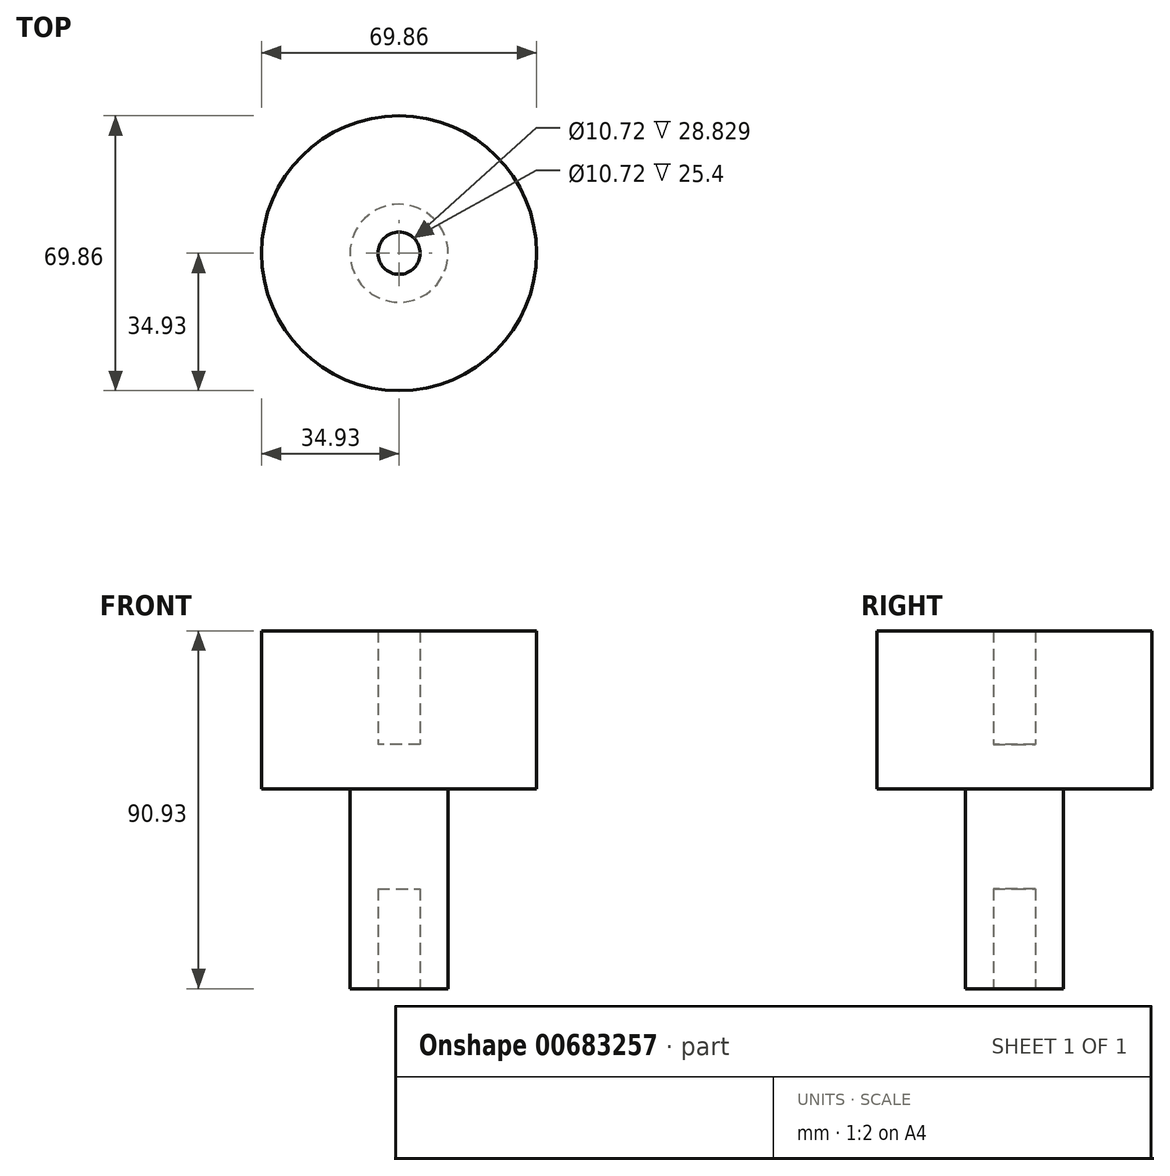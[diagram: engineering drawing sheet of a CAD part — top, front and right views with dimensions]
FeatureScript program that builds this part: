
annotation { "Feature Type Name" : "Feature", "Feature Type Description" : "" }
export const myFeature = defineFeature(function(context is Context, id is Id, definition is map)
    precondition{}
    {
        {
            var Q0;
            Q0=qCreatedBy(makeId("Top.planeOp"),FACE);
            var sketch = newSketch(context, id + "F0", { "sketchPlane" : qUnion([Q0])});
            skCircle(sketch, "E0", {"center": v(0, 0) * mm, "radius": 34.93 * mm});
            skCircle(sketch, "E1", {"center": v(0, 0) * mm, "radius": 5.36 * mm});
            skSolve(sketch);
        }
        {
            var Q0;
            Q0=makeQuery(id+"F0.imprint","IMPRINT",FACE,{"disambiguationData":[TD([[makeQuery(id+"F0.imprint","IMPRINT",EDGE,{"derivedFrom":sQuery(id+"F0.wireOp",EDGE,"E0")}),1.0]])]});
            extrude(context, id + "F1", {"entities" : qUnion([Q0]), "depth" : 40.13 * mm, "offsetDistance" : 25.4 * mm});
        }
        {
            var Q0;
            Q0=makeQuery(id+"F0.imprint","IMPRINT",FACE,{"disambiguationData":[TD([[makeQuery(id+"F0.imprint","IMPRINT",EDGE,{"derivedFrom":sQuery(id+"F0.wireOp",EDGE,"E1")}),1.0]])]});
            extrude(context, id + "F2", {"entities" : qUnion([Q0]), "operationType" : NewBodyOperationType.ADD, "depth" : 9.52 * mm, "offsetDistance" : 25.4 * mm});
        }
        {
            var Q0;
            Q0=makeQuery(id+"F0.imprint","IMPRINT",FACE,{"disambiguationData":[TD([[makeQuery(id+"F0.imprint","IMPRINT",EDGE,{"derivedFrom":sQuery(id+"F0.wireOp",EDGE,"E0")}),1.0]])]});
            var sketch = newSketch(context, id + "F3", { "sketchPlane" : qUnion([Q0])});
            skCircle(sketch, "E2", {"center": v(0, 0) * mm, "radius": 5.13 * mm});
            skSolve(sketch);
        }
        {
            var Q0;
            Q0=makeQuery(id+"F3.imprint","IMPRINT",FACE,{"disambiguationData":[TD([[makeQuery(id+"F3.imprint","IMPRINT",EDGE,{"derivedFrom":sQuery(id+"F3.wireOp",EDGE,"E2")}),1.0]])]});
            var sketch = newSketch(context, id + "F4", { "sketchPlane" : qUnion([Q0])});
            skCircle(sketch, "E3", {"center": v(0, 0) * mm, "radius": 12.46 * mm});
            skSolve(sketch);
        }
        {
            var Q0;
            Q0 = qSketchRegion(id + "F4", true);
            extrude(context, id + "F5", {"entities" : qUnion([Q0]), "operationType" : NewBodyOperationType.ADD, "oppositeDirection" : true, "depth" : 50.8 * mm, "offsetDistance" : 25.4 * mm});
        }
        {
            var Q0;
            Q0=makeQuery(id+"F5.opExtrude","CAP_FACE",FACE,{"disambiguationData":[OSD([sQuery(id+"F4.wireOp",EDGE,"E3")])],"isStart":false});
            var sketch = newSketch(context, id + "F6", { "sketchPlane" : qUnion([Q0])});
            skCircle(sketch, "E4", {"center": v(0, 0) * mm, "radius": 5.36 * mm});
            skSolve(sketch);
        }
        {
            var Q0;
            Q0 = qSketchRegion(id + "F6", true);
            extrude(context, id + "F7", {"entities" : qUnion([Q0]), "operationType" : NewBodyOperationType.REMOVE, "oppositeDirection" : true, "depth" : 25.4 * mm, "offsetDistance" : 25.4 * mm});
        }
        {
            var Q0;
            Q0=qCreatedBy(makeId("Top.planeOp"),FACE);
            var sketch = newSketch(context, id + "F8", { "sketchPlane" : qUnion([Q0])});
            skCircle(sketch, "E5", {"center": v(0, 0) * mm, "radius": 5.36 * mm});
            skSolve(sketch);
        }
        {
            var Q0;
            Q0 = qSketchRegion(id + "F8", true);
            extrude(context, id + "F9", {"entities" : qUnion([Q0]), "operationType" : NewBodyOperationType.ADD, "depth" : 11.3 * mm, "offsetDistance" : 25.4 * mm});
        }
    });
